# Revit family: Shower-Rainhead-KOHLER-Urbanity-K-33428T
name_source: partatom
category: Plumbing Fixtures
units: mm (PartAtom-declared; Revit-internal decimal feet)

## family parameters
Cut with Voids When Loaded = No
Host = Face
OmniClass Number = 23.31.17.00
Part Type = Normal
Room Calculation Point = No
Round Connector Dimension = Use Diameter
Shared = No

## types (13) — shared parameters
ADA Compliant = No
Assembly Code = D2010700
CW Connection = No
Cold Water Inlet = Cold Water Inlet
Date Modified = 09/12/2024
Default Elevation = 42"
Description = MF Rainhead 13 Inch With Water Mind
Flow Rate = 3 GPM
HW Connection = Yes
Height = 2 9/16"
Hot Water Inlet = Hot Water Inlet
Length = 9 3/16"
Manufacturer = Kohler Co.
Master Format 2014 = 22 42 23
Master Format 2014 Name = Residential Showers
Material = Premium Metal Construction
Pressure = 80.00 psi
Product Name = Urbanity
Tempered Water Inlet 1 = Tempered Water Inlet 1
Tempered Water Inlet 2 = Tempered Water Inlet 2
URL = http://www.kohler.com.cn
Vent Connection = No
Waste Connection = No
Waste Water Outlet = Waste Water Outlet
WaterSense Certified = No
Width = 13 3/16"

## per-type parameters (varying)
| type | Finish | Model | Type |
| 2MB-Vibrant Brushed Moderne Brass | Kohler-Metal-2MB-Vibrant_Brushed_Moderne_Brass | K-33428T-2MB | 1 |
| AF-Vibrant French Gold | Kohler-Metal-AF-Vibrant_French_Gold | K-33428T-AF | 2 |
| BL-Matte Black | Kohler-Metal-BL-Matte_Black | K-33428T-BL | 3 |
| BN-Vibrant Brushed Nickel | Kohler-Metal-BN-Vibrant_Brushed_Nickel | K-33428T-BN | 4 |
| BRD-Brushed Rose Gold | KOHLER-Metal-BRD-Brushed_Rose_Gold | K-33428T-BRD | 5 |
| BRT-Brushed Titanium | KOHLER-Metal-BRT-Brushed_Titanium | K-33428T-BRT | 6 |
| CP-Polished Chrome | Kohler-Metal-CP-Polished_Chrome | K-33428T-CP | 7 |
| RGD-Polished Rose Gold | Kohler-Metal-RGD-Polished_Rose_Gold | K-33428T-RGD | 8 |
| BGP-Brushed Graphite | Kohler-Metal-BGP-Brushed_Graphite | K-33428T-BGP | 9 |
| BV-Brushed Bronze | Kohler-Metal-BV-Brushed_Bronze | K-33428T-BV | 10 |
| PGP-Polished Graphite | Kohler-Metal-PGP-Polished_Graphite | K-33428T-PGP | 11 |
| SN-Vibrant Polished Nickel | Kohler-Metal-SN-Vibrant_Polished_Nickel | K-33428T-SN | 12 |
| TT-Vibrant Titanium | Kohler-Metal-TT-Vibrant_Titanium | K-33428T-TT | 13 |

## geometry (parser evidence)
native form markers: Sweep x3
no freeform markers — native parametric forms only
